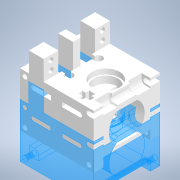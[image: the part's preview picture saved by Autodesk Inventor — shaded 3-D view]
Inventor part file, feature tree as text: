
AUTODESK INVENTOR PART (.ipt)
format: ipt  version: 2020 (Build 240168000, 168)  size: 572,928 bytes
history: native  units: mm
features: extrude x22, sketch x8, other x4, fillet x1
ambient origin geometry x8: Origin, YZ Plane, XZ Plane, XY Plane, X Axis, Y Axis, Z Axis, Center Point
bodies: Body1 (feature_tree)
feature tree (35):
  other  "Bryła1"
  extrude  "Wyciągnięcie proste1"  Depth=90.0mm
  sketch  "Szkic2"
  other  "Płaszczyzna konstrukcyjna1"
  extrude  "Wyciągnięcie proste2"  Depth=100.0mm
  extrude  "Wyciągnięcie proste3"  Depth=73.0mm TaperAngle=0.0deg
  sketch  "Szkic3"
  extrude  "Wyciągnięcie proste4"  Depth=6.5mm
  extrude  "Wyciągnięcie proste5"  Depth=6.5mm
  extrude  "Wyciągnięcie proste6"  Depth=6.5mm
  extrude  "Wyciągnięcie proste7"  Depth=6.5mm
  sketch  "Szkic4"
  extrude  "Wyciągnięcie proste8"  Depth=6.5mm
  extrude  "Wyciągnięcie proste9"  Depth=6.5mm
  extrude  "Wyciągnięcie proste10"  Depth=11.0mm
  extrude  "Wyciągnięcie proste11"  [1 undecoded]
  extrude  "Wyciągnięcie proste12"  Depth=64.0mm TaperAngle=0.0deg
  other  "Płaszczyzna konstrukcyjna2"
  extrude  "Wyciągnięcie proste13"  TaperAngle=0.0deg  [1 undecoded]
  extrude  "Wyciągnięcie proste14"  Depth=36.5mm
  extrude  "Wyciągnięcie proste15"  Depth=45.0mm
  extrude  "Wyciągnięcie proste16"  Depth=28.5mm
  extrude  "Wyciągnięcie proste17"  Depth=48.5mm
  sketch  "Szkic8"
  extrude  "Wyciągnięcie proste18"  Depth=40.0mm
  extrude  "Wyciągnięcie proste19"  Depth=20.0mm
  extrude  "Wyciągnięcie proste20"  Depth=38.0mm
  other  "Płaszczyzna konstrukcyjna3"
  extrude  "Wyciągnięcie proste21"  Depth=5.5mm
  extrude  "Wyciągnięcie proste22"  TaperAngle=45.0deg  [1 undecoded]
  fillet  "Zaokrąglenie1"  [1 undecoded]
  sketch  "Szkic1"
  sketch  "Szkic5"
  sketch  "Szkic6"
  sketch  "Szkic7"
note: 4 required parameter values undecoded (feature->parameter linkage not recoverable at this tier; creation-order binding heuristic only, values carry confidence <= 0.55)
